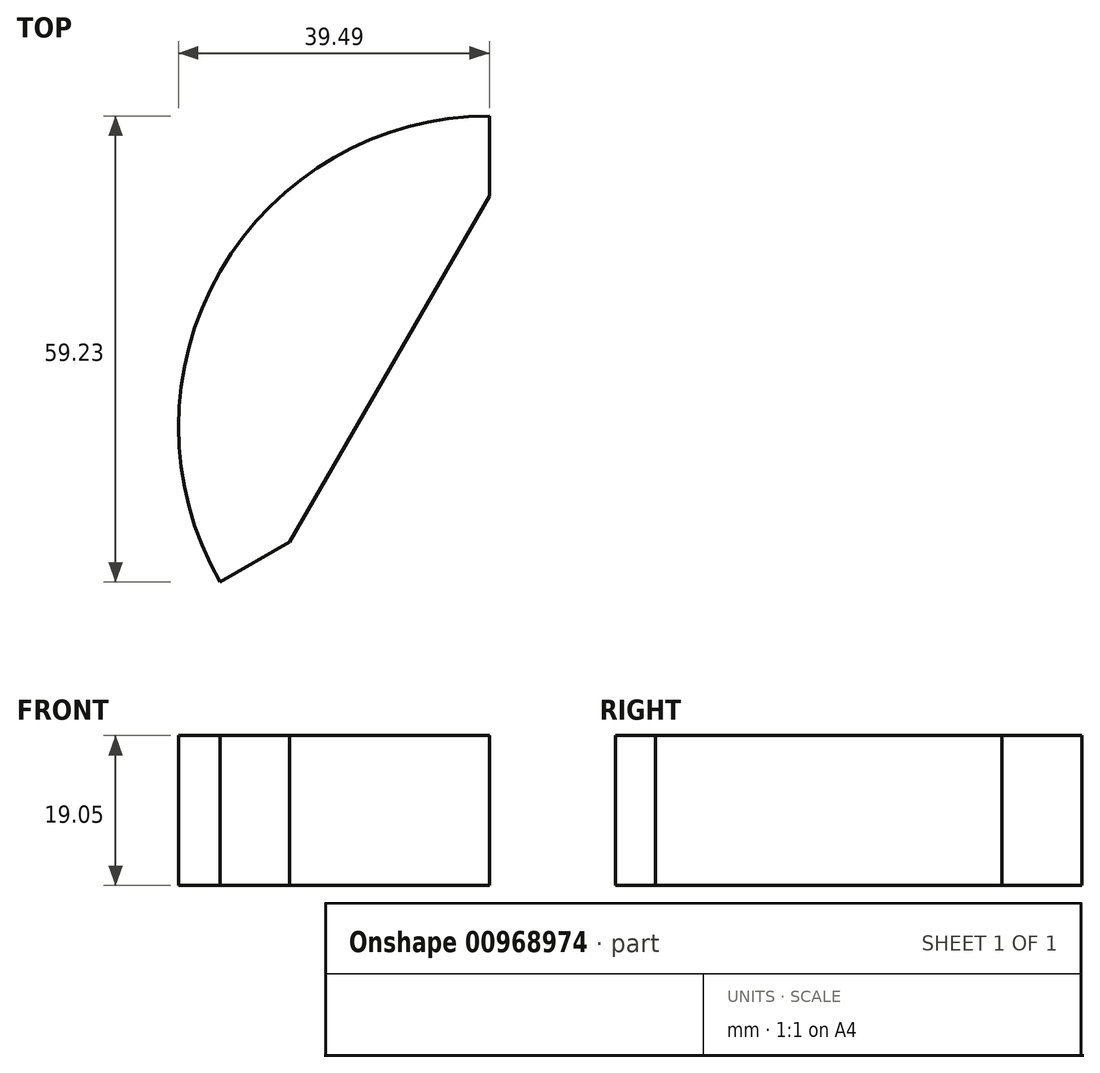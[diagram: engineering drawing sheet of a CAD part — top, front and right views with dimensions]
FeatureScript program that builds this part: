
annotation { "Feature Type Name" : "Feature", "Feature Type Description" : "" }
export const myFeature = defineFeature(function(context is Context, id is Id, definition is map)
    precondition{}
    {
        {
            var Q0;
            Q0=qCreatedBy(makeId("Top.planeOp"),FACE);
            var sketch = newSketch(context, id + "F0", { "sketchPlane" : qUnion([Q0])});
            skLineSegment(sketch, "E0", {"start": v(0, 10.16) * mm, "end": v(0, 0) * mm});
            skLineSegment(sketch, "E1", {"start": v(0, 0) * mm, "end": v(-25.4, -44) * mm});
            skLineSegment(sketch, "E2", {"start": v(-25.4, -44) * mm, "end": v(-34.2, -49.07) * mm});
            skArc(sketch, "E3", {"start": v(0, 10.16) * mm, "mid": v(-34.2, -9.58) * mm, "end": v(-34.2, -49.07) * mm});
            skSolve(sketch);
        }
        {
            var Q0;
            Q0=makeQuery(id+"F0.imprint","IMPRINT",FACE,{"disambiguationData":[TD([[makeQuery(id+"F0.imprint","IMPRINT",EDGE,{"derivedFrom":sQuery(id+"F0.wireOp",EDGE,"E0")}),-1.0]])]});
            extrude(context, id + "F1", {"entities" : qUnion([Q0]), "depth" : 19.05 * mm, "offsetDistance" : 25.4 * mm});
        }
    });
